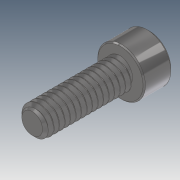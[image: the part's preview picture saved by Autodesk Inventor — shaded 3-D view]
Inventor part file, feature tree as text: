
AUTODESK INVENTOR PART (.ipt)
format: ipt  version: 2020.4 (Build 244396000, 396)  size: 678,400 bytes
history: native  units: in
note: dims shown in document units (in); Inventor stores cm internally (conversion verified against a paired STEP export)
features: chamfer x1
ambient origin geometry x8: Origin, YZ Plane, XZ Plane, XY Plane, X Axis, Y Axis, Z Axis, Center Point
bodies: Solid1 (feature_tree)
feature tree (1):
  chamfer  "Chamfer2"  [1 undecoded]
note: 1 required parameter value undecoded (feature->parameter linkage not recoverable at this tier; creation-order binding heuristic only, values carry confidence <= 0.55)
